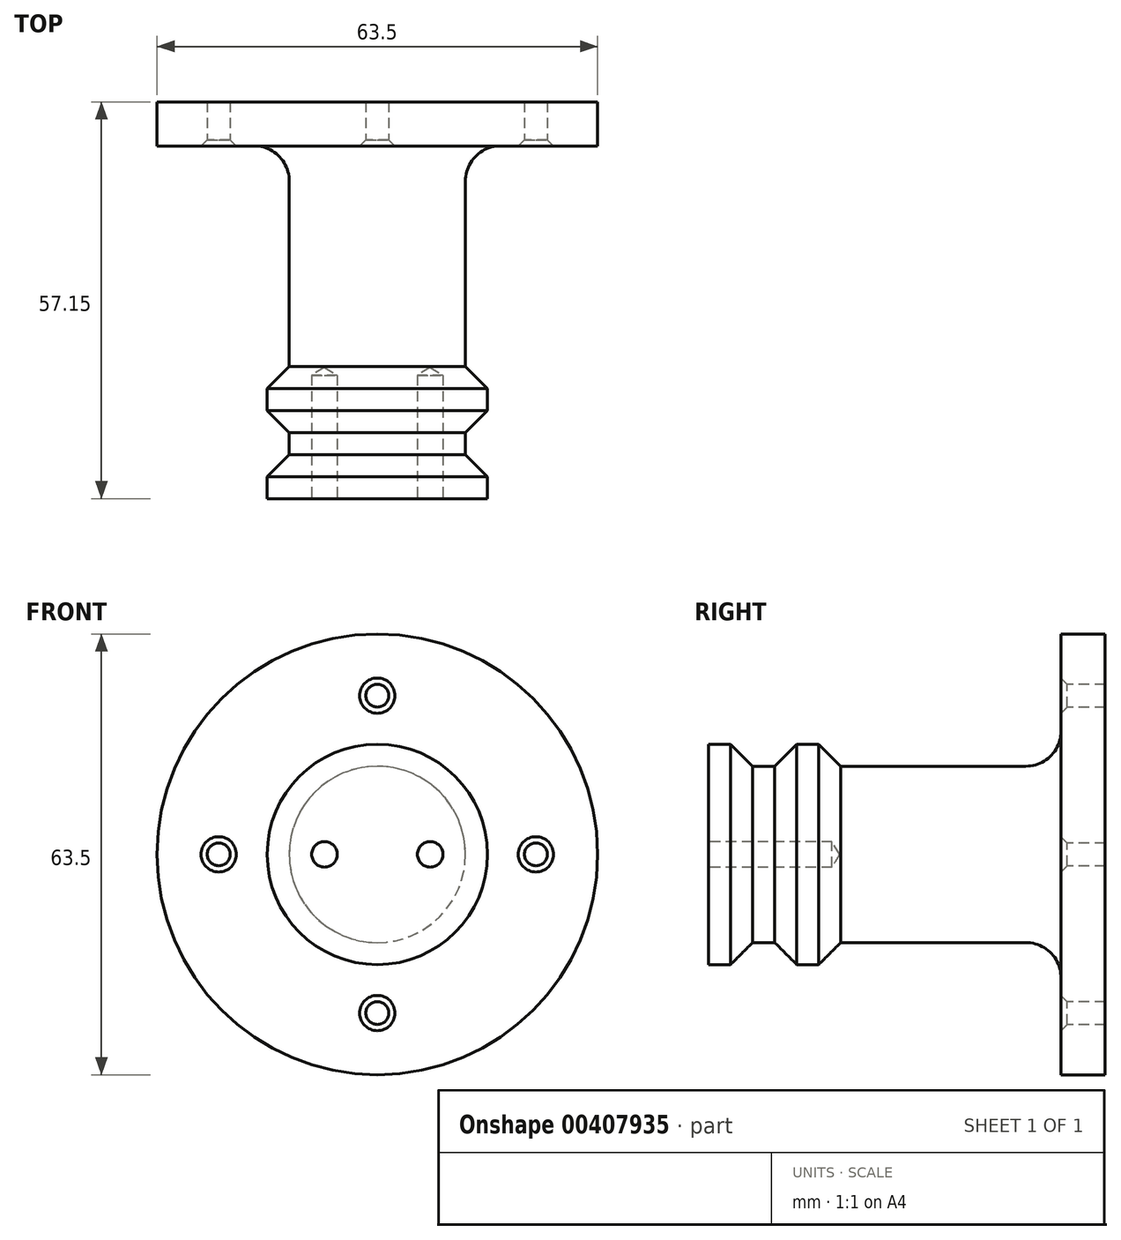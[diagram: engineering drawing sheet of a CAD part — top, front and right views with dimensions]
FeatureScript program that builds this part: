
annotation { "Feature Type Name" : "Feature", "Feature Type Description" : "" }
export const myFeature = defineFeature(function(context is Context, id is Id, definition is map)
    precondition{}
    {
        {
            var Q0;
            Q0=qCreatedBy(makeId("Right.planeOp"),FACE);
            var sketch = newSketch(context, id + "F0", { "sketchPlane" : qUnion([Q0])});
            skLineSegment(sketch, "E0", {"start": v(0, 0) * mm, "end": v(0, 31.75) * mm});
            skLineSegment(sketch, "E1", {"start": v(0, 31.75) * mm, "end": v(-6.35, 31.75) * mm});
            skLineSegment(sketch, "E2", {"start": v(-6.35, 31.75) * mm, "end": v(-6.35, 12.7) * mm});
            skLineSegment(sketch, "E3", {"start": v(-6.35, 12.7) * mm, "end": v(-38.1, 12.7) * mm});
            skLineSegment(sketch, "E4", {"start": v(-38.1, 12.7) * mm, "end": v(-41.27, 15.87) * mm});
            skLineSegment(sketch, "E5", {"start": v(-41.27, 15.87) * mm, "end": v(-44.45, 15.87) * mm});
            skLineSegment(sketch, "E6", {"start": v(-44.45, 15.87) * mm, "end": v(-47.62, 12.7) * mm});
            skLineSegment(sketch, "E7", {"start": v(-47.62, 12.7) * mm, "end": v(-50.8, 12.7) * mm});
            skLineSegment(sketch, "E8", {"start": v(-50.8, 12.7) * mm, "end": v(-53.97, 15.87) * mm});
            skLineSegment(sketch, "E9", {"start": v(-53.97, 15.87) * mm, "end": v(-57.15, 15.87) * mm});
            skLineSegment(sketch, "E10", {"start": v(-57.15, 15.87) * mm, "end": v(-57.15, 0) * mm});
            skLineSegment(sketch, "E11", {"start": v(-57.15, 0) * mm, "end": v(0, 0) * mm});
            skSolve(sketch);
        }
        {
            var Q0;
            Q0=makeQuery(id+"F0.imprint","IMPRINT",FACE,{"disambiguationData":[TD([[makeQuery(id+"F0.imprint","IMPRINT",EDGE,{"derivedFrom":sQuery(id+"F0.wireOp",EDGE,"E0")}),1.0]])]});
            var Q1;
            Q1=sQuery(id+"F0.wireOp",EDGE,"E11");
            revolve(context, id + "F1", {"entities" : qUnion([Q0]), "axis" : qUnion([Q1]), "revolveType" : RevolveType.FULL});
        }
        {
            var Q0;
            Q0=makeQuery(id+"F1.opRevolve","SWEPT_FACE",FACE,{"disambiguationData":[OSD([sQuery(id+"F0.wireOp",EDGE,"E2")])]});
            var sketch = newSketch(context, id + "F2", { "sketchPlane" : qUnion([Q0])});
            skCircle(sketch, "E12", {"center": v(0, 0) * mm, "radius": 22.86 * mm, "construction": true});
            skPoint(sketch, "E13", {"position": v(0, 22.86) * mm});
            skPoint(sketch, "E14", {"position": v(22.86, 0) * mm});
            skPoint(sketch, "E15", {"position": v(0, -22.86) * mm});
            skPoint(sketch, "E16", {"position": v(-22.86, 0) * mm});
            skSolve(sketch);
        }
        {
            var Q0;
            Q0=sQuery(id+"F2.wireOp",VERTEX,"E13");
            var Q1;
            Q1=sQuery(id+"F2.wireOp",VERTEX,"E14");
            var Q2;
            Q2=sQuery(id+"F2.wireOp",VERTEX,"E15");
            var Q3;
            Q3=sQuery(id+"F2.wireOp",VERTEX,"E16");
            var Q4;
            Q4=makeQuery(id+"F1.opRevolve","SWEPT_BODY",BODY,{"disambiguationData":[OSD([sQuery(id+"F0.wireOp",EDGE,"E0"),sQuery(id+"F0.wireOp",EDGE,"E1"),sQuery(id+"F0.wireOp",EDGE,"E2"),sQuery(id+"F0.wireOp",EDGE,"E3"),sQuery(id+"F0.wireOp",EDGE,"E4"),sQuery(id+"F0.wireOp",EDGE,"E5"),sQuery(id+"F0.wireOp",EDGE,"E6"),sQuery(id+"F0.wireOp",EDGE,"E7"),sQuery(id+"F0.wireOp",EDGE,"E8"),sQuery(id+"F0.wireOp",EDGE,"E9"),sQuery(id+"F0.wireOp",EDGE,"E10"),sQuery(id+"F0.wireOp",EDGE,"E11")])]});
            hole(context, id + "F3", {"style" : HoleStyle.C_SINK, "endStyle" : HoleEndStyle.THROUGH, "holeDiameter" : 3.3 * mm, "cSinkDiameter" : 5.08 * mm, "cSinkAngle" : 90 * degree, "isTappedThrough" : true, "tappedDepth" : 12.7 * mm, "tapClearance" : 3, "startFromSketch" : true, "locations" : qUnion([Q0, Q1, Q2, Q3]), "scope" : qUnion([Q4])});
        }
        {
            var Q0;
            Q0=makeQuery(id+"F1.opRevolve","SWEPT_FACE",FACE,{"disambiguationData":[OSD([sQuery(id+"F0.wireOp",EDGE,"E10")])]});
            var sketch = newSketch(context, id + "F4", { "sketchPlane" : qUnion([Q0])});
            skCircle(sketch, "E17", {"center": v(0, 0) * mm, "radius": 7.62 * mm, "construction": true});
            skPoint(sketch, "E18", {"position": v(-7.62, 0) * mm});
            skPoint(sketch, "E19", {"position": v(7.62, 0) * mm});
            skSolve(sketch);
        }
        {
            var Q0;
            Q0=sQuery(id+"F4.wireOp",VERTEX,"E18");
            var Q1;
            Q1=sQuery(id+"F4.wireOp",VERTEX,"E19");
            var Q2;
            Q2=makeQuery(id+"F1.opRevolve","SWEPT_BODY",BODY,{"disambiguationData":[OSD([sQuery(id+"F0.wireOp",EDGE,"E0"),sQuery(id+"F0.wireOp",EDGE,"E1"),sQuery(id+"F0.wireOp",EDGE,"E2"),sQuery(id+"F0.wireOp",EDGE,"E3"),sQuery(id+"F0.wireOp",EDGE,"E4"),sQuery(id+"F0.wireOp",EDGE,"E5"),sQuery(id+"F0.wireOp",EDGE,"E6"),sQuery(id+"F0.wireOp",EDGE,"E7"),sQuery(id+"F0.wireOp",EDGE,"E8"),sQuery(id+"F0.wireOp",EDGE,"E9"),sQuery(id+"F0.wireOp",EDGE,"E10"),sQuery(id+"F0.wireOp",EDGE,"E11")])]});
            hole(context, id + "F5", {"style" : HoleStyle.SIMPLE, "endStyle" : HoleEndStyle.BLIND, "holeDiameter" : 3.68 * mm, "holeDepth" : 17.78 * mm, "isTappedThrough" : true, "tappedDepth" : 12.7 * mm, "tapClearance" : 3, "startFromSketch" : true, "locations" : qUnion([Q0, Q1]), "scope" : qUnion([Q2])});
        }
        {
            var Q0;
            Q0=makeQuery(id+"F1.opRevolve","SWEPT_EDGE",EDGE,{"disambiguationData":[OSD([sQuery(id+"F0.wireOp",EDGE,"E2"),sQuery(id+"F0.wireOp",EDGE,"E3")])]});
            fillet(context, id + "F6", {"entities" : qUnion([Q0]), "radius" : 5.08 * mm, "tangentPropagation" : true, "allowEdgeOverflow" : false});
        }
    });
